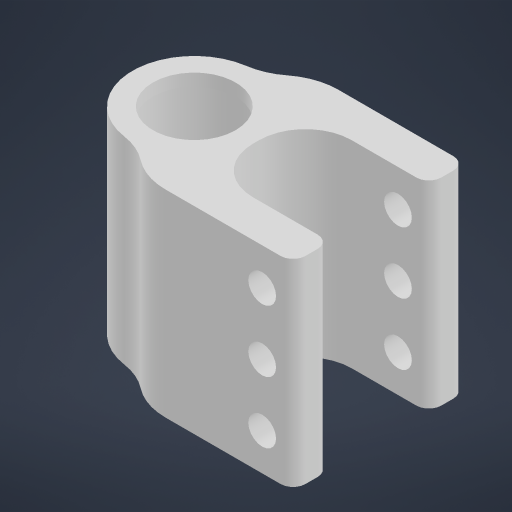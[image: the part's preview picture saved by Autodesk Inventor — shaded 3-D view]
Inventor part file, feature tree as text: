
AUTODESK INVENTOR PART (.ipt)
format: ipt  version: 2024.1 (Build 281209000, 209)  size: 279,040 bytes
history: native  units: mm
features: fillet x5, extrude x4, sketch x3
ambient origin geometry x8: Origin, YZ Plane, XZ Plane, XY Plane, X Axis, Y Axis, Z Axis, Center Point
bodies: Solid1 (feature_tree)
feature tree (12):
  sketch  "Sketch1"  dims[d0=13.4mm d1=15.4mm]
  extrude  "Extrusion1"  Depth=15.4mm
  extrude  "Extrusion2"  Depth=30.0mm TaperAngle=0.0deg
  extrude  "Extrusion3"  Depth=10.0mm
  fillet  "Fillet2"  Radius=62.5mm
  extrude  "Extrusion7"  Depth=7.5mm
  fillet  "Fillet5"  Radius=4.5mm
  fillet  "Fillet6"  Radius=10.0mm
  fillet  "Fillet7"  Radius=30.0mm
  fillet  "Fillet4"  Radius=20.0mm
  sketch  "Sketch2"  dims[d3=2.0mm d4=0.0mm d5=30.0mm d6=0.0mm]
  sketch  "Sketch4"  dims[d7=3.5mm d8=5.0mm d9=62.5mm d10=0.0mm d31=7.5mm d32=4.5mm d33=10.0mm d35=30.0mm d36=0.0mm d37=20.0mm d38=20.0mm d39=6.0mm d40=5.0mm d41=5.0mm d43=2.0mm d46=16.0mm d47=10.0mm d48=10.0mm d49=10.0mm]
